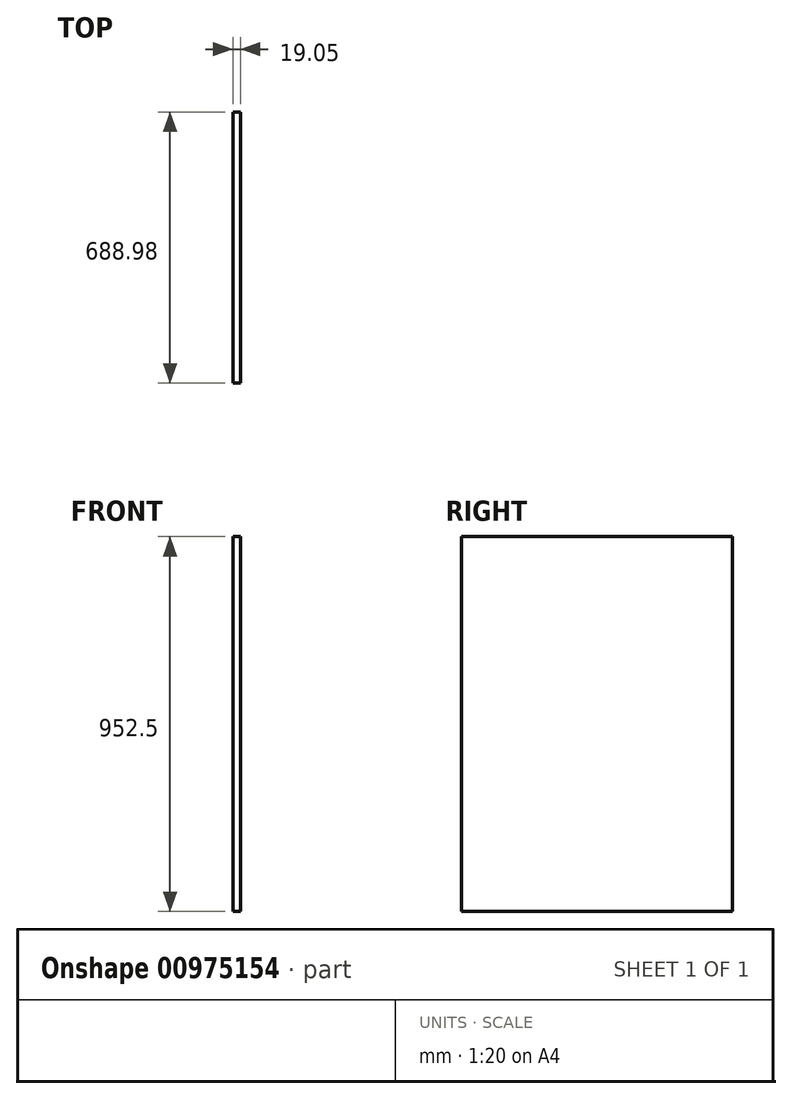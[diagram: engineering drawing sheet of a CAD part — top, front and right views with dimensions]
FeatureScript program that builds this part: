
annotation { "Feature Type Name" : "Feature", "Feature Type Description" : "" }
export const myFeature = defineFeature(function(context is Context, id is Id, definition is map)
    precondition{}
    {
        {
            var Q0;
            Q0=qCreatedBy(makeId("Right.planeOp"),FACE);
            var sketch = newSketch(context, id + "F0", { "sketchPlane" : qUnion([Q0])});
            skLineSegment(sketch, "E0.bottom", {"start": v(0, 0) * mm, "end": v(688.98, 0) * mm});
            skLineSegment(sketch, "E0.top", {"start": v(0, 952.5) * mm, "end": v(688.97, 952.5) * mm});
            skLineSegment(sketch, "E0.left", {"start": v(0, 0) * mm, "end": v(0, 952.5) * mm});
            skLineSegment(sketch, "E0.right", {"start": v(688.98, 0) * mm, "end": v(688.97, 952.5) * mm});
            skSolve(sketch);
        }
        {
            var Q0;
            Q0=makeQuery(id+"F0.imprint","IMPRINT",FACE,{"disambiguationData":[TD([[makeQuery(id+"F0.imprint","IMPRINT",EDGE,{"derivedFrom":sQuery(id+"F0.wireOp",EDGE,"E0.bottom")}),1.0]])]});
            extrude(context, id + "F1", {"entities" : qUnion([Q0]), "depth" : 19.05 * mm, "offsetDistance" : 25.4 * mm});
        }
    });
